# Revit family: Plumbing Fixture-Grease_Interseptor_Mifab_MI-E-G
name_source: partatom
category: Plumbing Fixtures
revit_build: Autodesk Revit Structure 2013 (Build: 20120221_2030(x64)
units: mm (PartAtom-declared; Revit-internal decimal feet)

## types (8) — shared parameters
Assembly Code = D2090300
C = 7.5 "
Description = Electronic Grease Interceptor
F = 4 "
Interceptor Material = Acid Resistant Epoxy Coated Green
Manufacturer = MIFAB
Standard Inlet And Outlet Radii = 2 "
URL = www.mifab.com
zero-valued in all types: Default Elevation, WFU

## per-type parameters (varying)
| type | A | B | D | E | Flow Rate | Grease Capacity | Water Capacity |
| MI-E-G-0 | 16.75 " | 11.25 " | 8.5 " | 16 " | 4 GPM | 8 lbs | 4.43 Gallons |
| MI-E-G-1 | 17.75 " | 13.75 " | 8.5 " | 16 " | 7 GPM | 14 lbs | 6 Gallons |
| MI-E-G-2 | 21.25 " | 15.75 " | 9.5 " | 17 " | 10 GPM | 20 lbs | 9.74 Gallons |
| MI-E-G-3 | 23.75 " | 15.75 " | 11.5 " | 19 " | 15 GPM | 30 lbs | 13.59 Gallons |
| MI-E-G-4 | 23.75 " | 15.75 " | 14 " | 21.5 " | 20 GPM | 40 lbs | 16.18 Gallons |
| MI-E-G-5 | 27.75 " | 18.75 " | 14 " | 21.5 " | 25 GPM | 50 lbs | 23.34 Gallons |
| MI-E-G-6 | 31.25 " | 23.75 " | 16.5 " | 24 " | 35 GPM | 70 lbs | 41.31 Gallons |
| MI-E-G-7 | 31.25 " | 23.75 " | 16.5 " | 26 " | 50 GPM | 100 lbs | 46.82 Gallons |

note: column(s) folded — value = type name in every type: Model

## geometry (parser evidence)
native form markers: Blend x7, Sweep x1
no freeform markers — native parametric forms only
